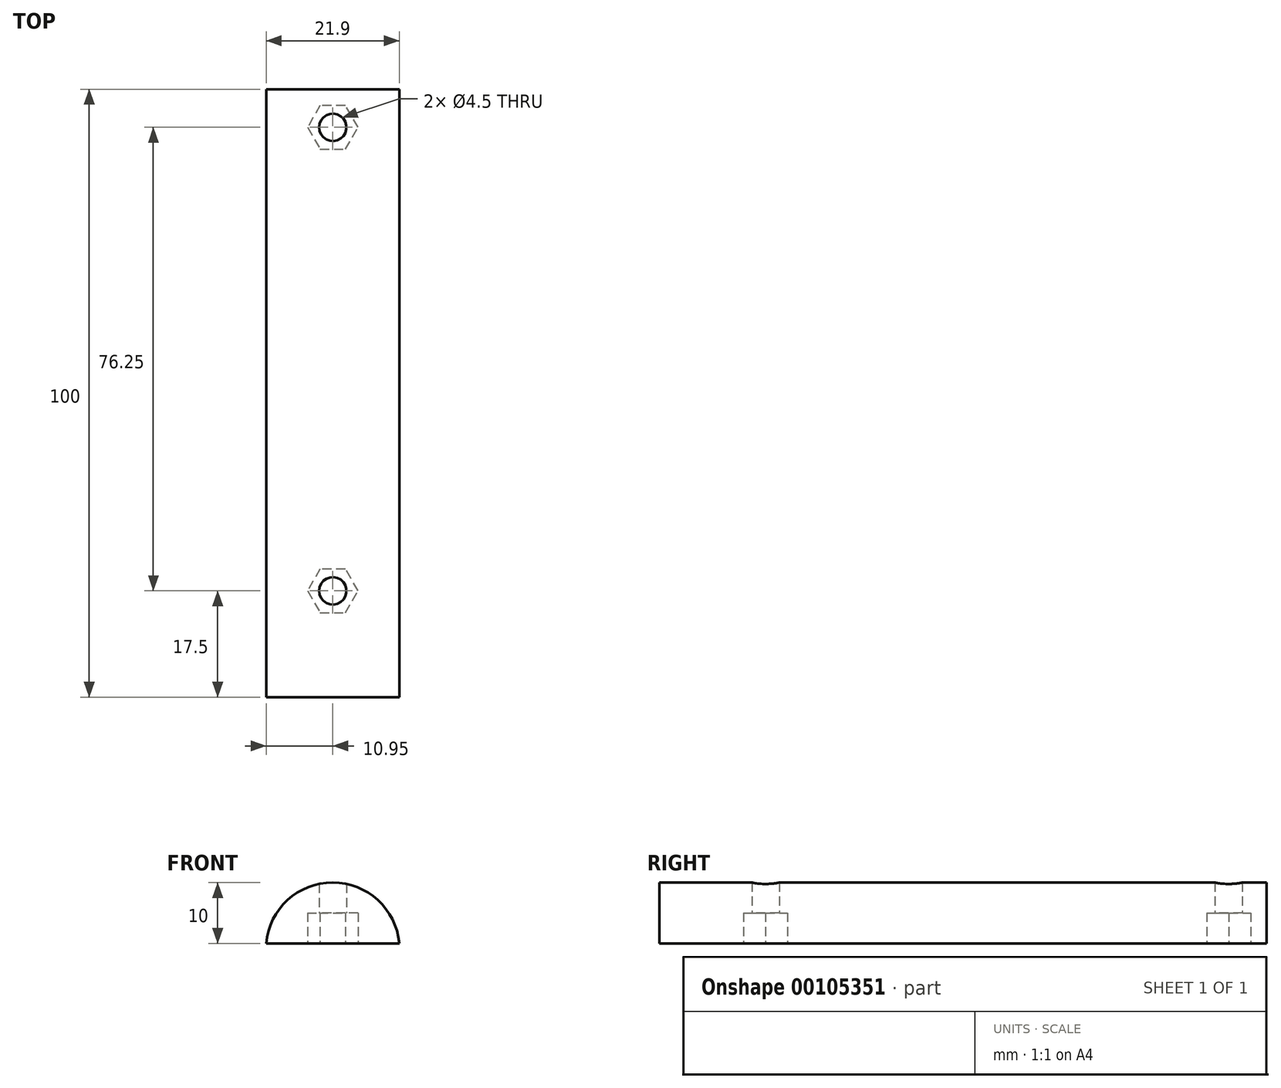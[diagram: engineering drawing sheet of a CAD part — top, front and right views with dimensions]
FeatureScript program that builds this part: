
annotation { "Feature Type Name" : "Feature", "Feature Type Description" : "" }
export const myFeature = defineFeature(function(context is Context, id is Id, definition is map)
    precondition{}
    {
        {
            var Q0;
            Q0=qCreatedBy(makeId("Front.planeOp"),FACE);
            var sketch = newSketch(context, id + "F0", { "sketchPlane" : qUnion([Q0])});
            skArc(sketch, "E0", {"start": v(-11, 0) * mm, "mid": v(0, 11) * mm, "end": v(11, 0) * mm});
            skLineSegment(sketch, "E1", {"start": v(-10.95, 1) * mm, "end": v(10.95, 1) * mm});
            skPoint(sketch, "E2", {"position": v(0, 11) * mm});
            skSolve(sketch);
        }
        {
            var Q0;
            Q0 = qSketchRegion(id + "F0", true);
            extrude(context, id + "F1", {"entities" : qUnion([Q0]), "depth" : 100 * mm});
        }
        {
            var Q0;
            Q0=makeQuery(id+"F1.opExtrude","SWEPT_FACE",FACE,{"disambiguationData":[OSD([sQuery(id+"F0.wireOp",EDGE,"E1")])]});
            var sketch = newSketch(context, id + "F2", { "sketchPlane" : qUnion([Q0])});
            skLineSegment(sketch, "E3", {"start": v(0, 100) * mm, "end": v(0, 0) * mm, "construction": true});
            skCircle(sketch, "E4", {"center": v(0, 6.25) * mm, "radius": 2.25 * mm});
            skCircle(sketch, "E5", {"center": v(0, 82.5) * mm, "radius": 2.25 * mm});
            skCircle(sketch, "E6.cCircle", {"center": v(0, 6.25) * mm, "radius": 3.6 * mm, "construction": true});
            skLineSegment(sketch, "E6.0", {"start": v(2.08, 2.65) * mm, "end": v(-2.08, 2.65) * mm});
            skLineSegment(sketch, "E6.1", {"start": v(-2.08, 2.65) * mm, "end": v(-4.16, 6.25) * mm});
            skLineSegment(sketch, "E6.2", {"start": v(-4.16, 6.25) * mm, "end": v(-2.08, 9.85) * mm});
            skLineSegment(sketch, "E6.3", {"start": v(-2.08, 9.85) * mm, "end": v(2.08, 9.85) * mm});
            skLineSegment(sketch, "E6.4", {"start": v(2.08, 9.85) * mm, "end": v(4.16, 6.25) * mm});
            skLineSegment(sketch, "E6.5", {"start": v(4.16, 6.25) * mm, "end": v(2.08, 2.65) * mm});
            skPoint(sketch, "E6.0.midPoint", {"position": v(0, 2.65) * mm});
            skCircle(sketch, "E7.cCircle", {"center": v(0, 82.5) * mm, "radius": 3.6 * mm, "construction": true});
            skLineSegment(sketch, "E7.0", {"start": v(2.08, 78.9) * mm, "end": v(-2.08, 78.9) * mm});
            skLineSegment(sketch, "E7.1", {"start": v(-2.08, 78.9) * mm, "end": v(-4.16, 82.5) * mm});
            skLineSegment(sketch, "E7.2", {"start": v(-4.16, 82.5) * mm, "end": v(-2.08, 86.1) * mm});
            skLineSegment(sketch, "E7.3", {"start": v(-2.08, 86.1) * mm, "end": v(2.08, 86.1) * mm});
            skLineSegment(sketch, "E7.4", {"start": v(2.08, 86.1) * mm, "end": v(4.16, 82.5) * mm});
            skLineSegment(sketch, "E7.5", {"start": v(4.16, 82.5) * mm, "end": v(2.08, 78.9) * mm});
            skPoint(sketch, "E7.0.midPoint", {"position": v(0, 78.9) * mm});
            skSolve(sketch);
        }
        {
            var Q0;
            Q0 = qSketchRegion(id + "F2", true);
            extrude(context, id + "F3", {"entities" : qUnion([Q0]), "operationType" : NewBodyOperationType.REMOVE, "oppositeDirection" : true, "depth" : 5 * mm});
        }
        {
            var Q0;
            Q0=makeQuery(id+"F3.boolean.opBoolean","SPLIT",FACE,{"disambiguationData":[TD([makeQuery(id+"F3.opExtrude","SWEPT_FACE",FACE,{"disambiguationData":[OSD([sQuery(id+"F2.wireOp",EDGE,"E5")])]})])],"derivedFrom":makeQuery(id+"F1.opExtrude","SWEPT_FACE",FACE,{"disambiguationData":[OSD([sQuery(id+"F0.wireOp",EDGE,"E1")])]})});
            var Q1;
            Q1=makeQuery(id+"F3.boolean.opBoolean","SPLIT",FACE,{"disambiguationData":[TD([makeQuery(id+"F3.opExtrude","SWEPT_FACE",FACE,{"disambiguationData":[OSD([sQuery(id+"F2.wireOp",EDGE,"E4")])]})])],"derivedFrom":makeQuery(id+"F1.opExtrude","SWEPT_FACE",FACE,{"disambiguationData":[OSD([sQuery(id+"F0.wireOp",EDGE,"E1")])]})});
            extrude(context, id + "F4", {"entities" : qUnion([Q0, Q1]), "operationType" : NewBodyOperationType.REMOVE, "oppositeDirection" : true, "depth" : 25 * mm});
        }
    });
